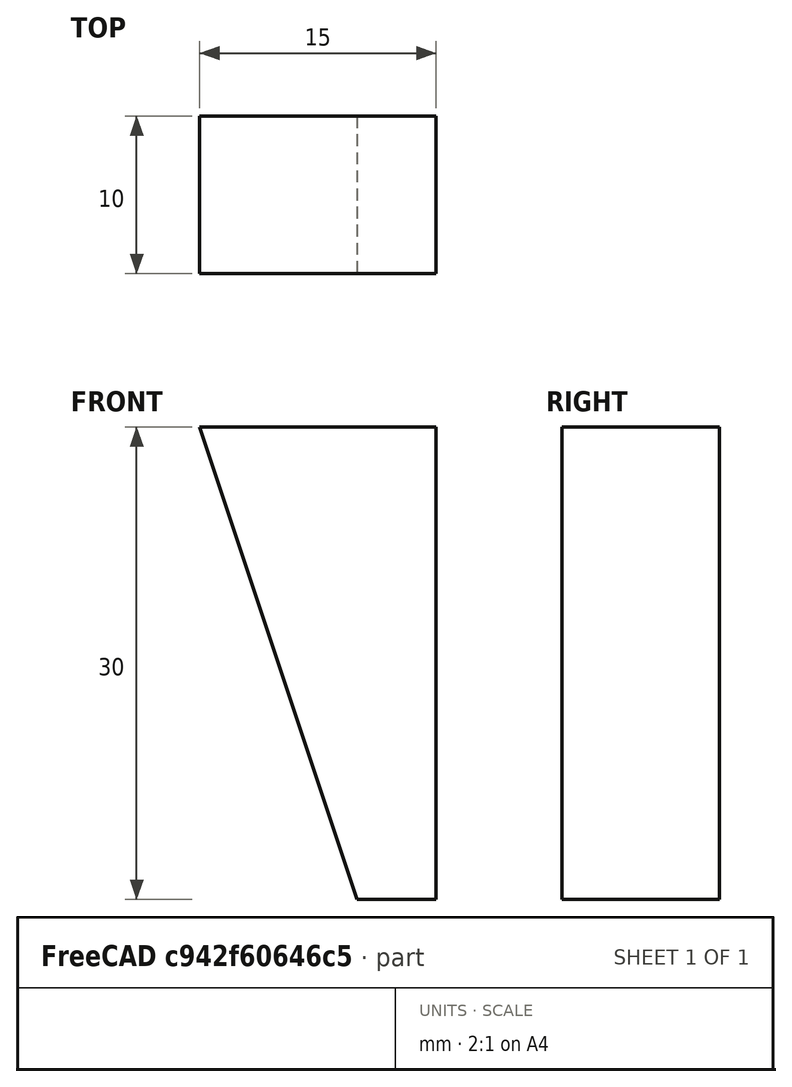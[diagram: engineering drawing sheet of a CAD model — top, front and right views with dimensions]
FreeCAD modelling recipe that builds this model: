
FCSTD DOCUMENT  (FreeCAD 0.18.4R)
Label: gripper-arm
License: All rights reserved
LicenseURL: http://en.wikipedia.org/wiki/All_rights_reserved
objects: Sketcher::SketchObject×1, PartDesign::Pad×1, PartDesign::Body×1
note: 4 computed .brp shape members not serialized (recipe doc carries the construction recipe); baked Part::Feature solids carry a one-line shape summary decoded from their .brp

FEATURE [Sketcher::SketchObject] Sketch
  MapMode = 5
  Placement = pos=(0,0,0) rot=(1,0,0;1.5708rad)
  Support = -> [XZ_Plane]
  sketch-geometry (4):
    g0: LineSegment StartX=0 StartY=0 StartZ=0 EndX=0 EndY=-30 EndZ=0
    g1: LineSegment StartX=0 StartY=-30 StartZ=0 EndX=-5 EndY=-30 EndZ=0
    g2: LineSegment StartX=-5 StartY=-30 StartZ=0 EndX=-15 EndY=0 EndZ=0
    g3: LineSegment StartX=-15 StartY=0 StartZ=0 EndX=0 EndY=0 EndZ=0
  constraints (9):
    c: Coincident(g-1,g0)
    c: Vertical(g0)
    c: Coincident(g0,g1)
    c: Horizontal(g1)
    c: Coincident(g1,g2)
    c: Coincident(g2,g3)
    c: Coincident(g3,g0)
    c: Horizontal(g3)
    c: DistanceY(g0,g0) = 30
FEATURE [PartDesign::Pad] Pad
  Length = 10
  Length2 = 100
  Midplane = true
  Placement = pos=(0,0,0) rot=(1,0,0;1.5708rad)
  Profile = -> Sketch
  Type = 0
FEATURE [PartDesign::Body] Body
  Group = -> [Sketch,Pad]
  Origin = -> Origin
  Tip = -> Pad
